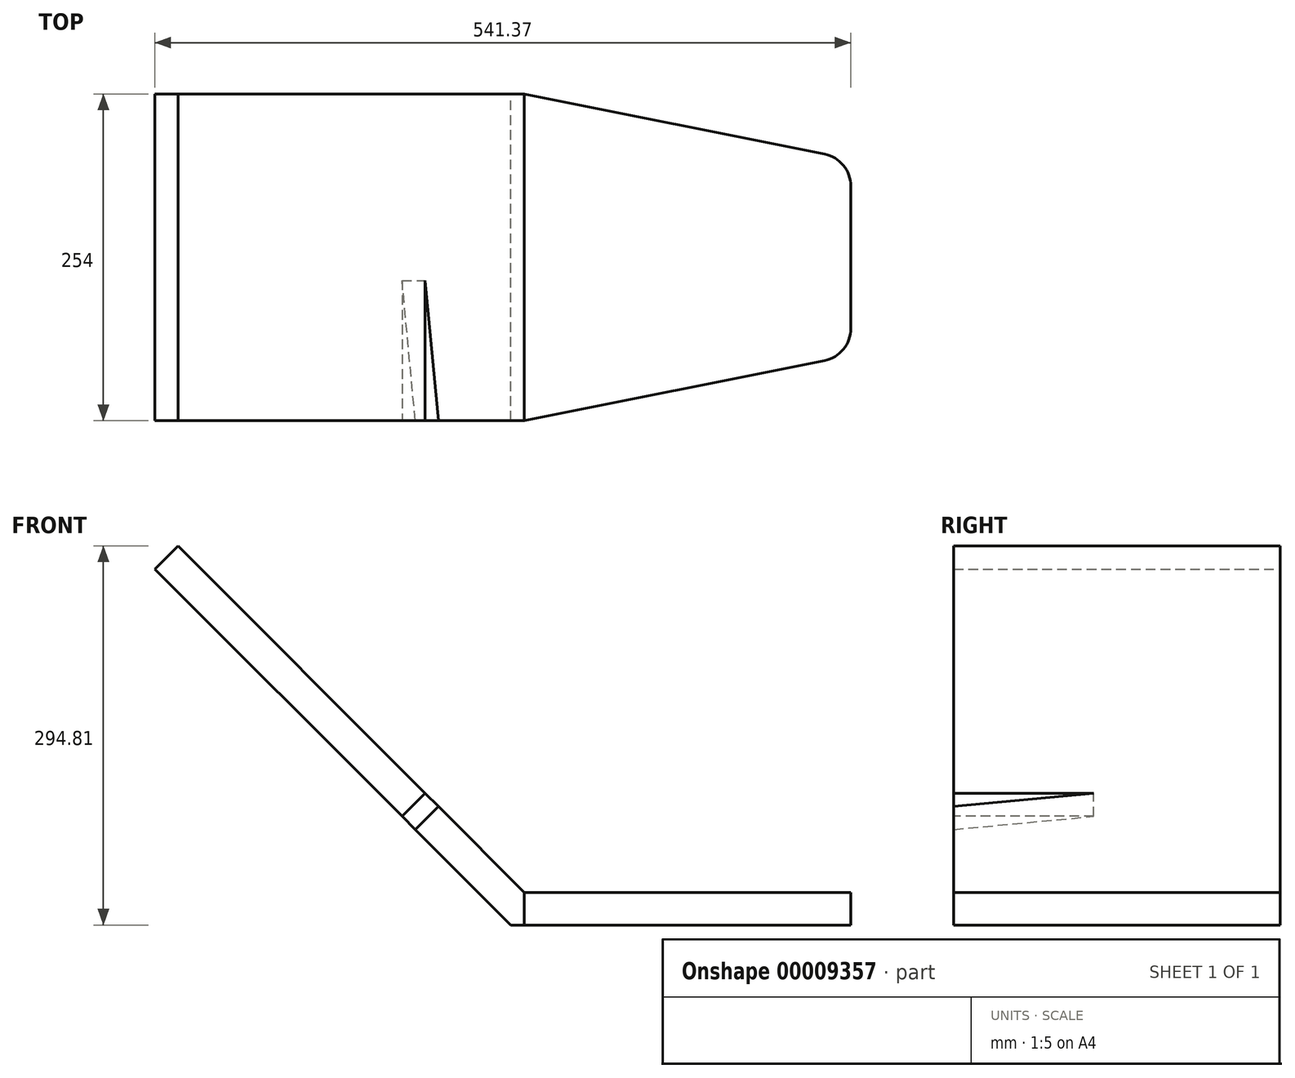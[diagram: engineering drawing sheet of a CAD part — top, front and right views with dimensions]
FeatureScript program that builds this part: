
annotation { "Feature Type Name" : "Feature", "Feature Type Description" : "" }
export const myFeature = defineFeature(function(context is Context, id is Id, definition is map)
    precondition{}
    {
        {
            var Q0;
            Q0=qCreatedBy(makeId("Top.planeOp"),FACE);
            var sketch = newSketch(context, id + "F0", { "sketchPlane" : qUnion([Q0])});
            skLineSegment(sketch, "E0", {"start": v(0, 127) * mm, "end": v(0, -127) * mm});
            skLineSegment(sketch, "E1", {"start": v(0, -127) * mm, "end": v(254, -76.2) * mm});
            skLineSegment(sketch, "E2", {"start": v(254, -76.2) * mm, "end": v(254, 76.2) * mm});
            skLineSegment(sketch, "E3", {"start": v(254, 76.2) * mm, "end": v(0, 127) * mm});
            skSolve(sketch);
        }
        {
            var Q0;
            Q0 = qSketchRegion(id + "F0", true);
            extrude(context, id + "F1", {"entities" : qUnion([Q0]), "depth" : 25.4 * mm});
        }
        {
            var Q0;
            Q0=qCreatedBy(makeId("Front.planeOp"),FACE);
            var sketch = newSketch(context, id + "F2", { "sketchPlane" : qUnion([Q0])});
            skLineSegment(sketch, "E4", {"start": v(0, 25.4) * mm, "end": v(-269.4, 294.8) * mm});
            skLineSegment(sketch, "E5", {"start": v(-269.4, 294.8) * mm, "end": v(-287.37, 276.85) * mm});
            skLineSegment(sketch, "E6", {"start": v(-287.37, 276.85) * mm, "end": v(-10.52, 0) * mm});
            skLineSegment(sketch, "E7", {"start": v(-10.52, 0) * mm, "end": v(0, 0) * mm});
            skLineSegment(sketch, "E8", {"start": v(0, 0) * mm, "end": v(0, 25.4) * mm});
            skSolve(sketch);
        }
        {
            var Q0;
            Q0=makeQuery(id+"F2.imprint","IMPRINT",FACE,{"disambiguationData":[TD([[makeQuery(id+"F2.imprint","IMPRINT",EDGE,{"derivedFrom":sQuery(id+"F2.wireOp",EDGE,"E4")}),1.0]])]});
            var Q1;
            Q1=makeQuery(id+"F1.opExtrude","SWEPT_FACE",FACE,{"disambiguationData":[OSD([sQuery(id+"F0.wireOp",EDGE,"E3")])]});
            extrude(context, id + "F3", {"entities" : qUnion([Q0]), "operationType" : NewBodyOperationType.ADD, "endBound" : BoundingType.SYMMETRIC, "endBoundEntityFace" : qUnion([Q1]), "depth" : 254 * mm});
        }
        {
            var Q0;
            Q0=makeQuery(id+"F3.opExtrude","SWEPT_FACE",FACE,{"disambiguationData":[OSD([sQuery(id+"F2.wireOp",EDGE,"E4")])]});
            var sketch = newSketch(context, id + "F4", { "sketchPlane" : qUnion([Q0])});
            skLineSegment(sketch, "E9", {"start": v(-398.96, 0) * mm, "end": v(-17.96, 0) * mm, "construction": true});
            skLineSegment(sketch, "E10", {"start": v(-398.96, -76.2) * mm, "end": v(-17.96, -127) * mm});
            skLineSegment(sketch, "E11", {"start": v(-17.96, -127) * mm, "end": v(-398.96, -127) * mm});
            skLineSegment(sketch, "E12", {"start": v(-398.96, -127) * mm, "end": v(-398.96, -76.2) * mm});
            skLineSegment(sketch, "E13.MirrorCS", {"start": v(-398.96, 76.2) * mm, "end": v(-17.96, 127) * mm});
            skLineSegment(sketch, "E14.MirrorCS", {"start": v(-398.96, 127) * mm, "end": v(-398.96, 76.2) * mm});
            skLineSegment(sketch, "E15.MirrorCS", {"start": v(-17.96, 127) * mm, "end": v(-398.96, 127) * mm});
            skSolve(sketch);
        }
        {
            var Q0;
            Q0 = qSketchRegion(id + "F4", true);
            extrude(context, id + "F5", {"entities" : qUnion([Q0]), "operationType" : NewBodyOperationType.REMOVE, "endBound" : BoundingType.THROUGH_ALL, "oppositeDirection" : true, "depth" : 25.4 * mm});
        }
        {
            var Q0;
            Q0=makeQuery(id+"F5.boolean.opBoolean","COPY",EDGE,{"derivedFrom":makeQuery(id+"F5.opExtrude","SWEPT_EDGE",EDGE,{"disambiguationData":[OSD([sQuery(id+"F2.wireOp",EDGE,"E4"),sQuery(id+"F2.wireOp",EDGE,"E5"),sQuery(id+"F4.wireOp",EDGE,"E10"),sQuery(id+"F4.wireOp",EDGE,"E12")])]})});
            var Q1;
            Q1=makeQuery(id+"F5.boolean.opBoolean","COPY",EDGE,{"derivedFrom":makeQuery(id+"F5.opExtrude","SWEPT_EDGE",EDGE,{"disambiguationData":[OSD([sQuery(id+"F2.wireOp",EDGE,"E4"),sQuery(id+"F2.wireOp",EDGE,"E5"),sQuery(id+"F4.wireOp",EDGE,"E13.MirrorCS"),sQuery(id+"F4.wireOp",EDGE,"E14.MirrorCS")])]})});
            var Q2;
            Q2=makeQuery(id+"F1.opExtrude","SWEPT_EDGE",EDGE,{"disambiguationData":[OSD([sQuery(id+"F0.wireOp",EDGE,"E1"),sQuery(id+"F0.wireOp",EDGE,"E2")])]});
            var Q3;
            Q3=makeQuery(id+"F1.opExtrude","SWEPT_EDGE",EDGE,{"disambiguationData":[OSD([sQuery(id+"F0.wireOp",EDGE,"E2"),sQuery(id+"F0.wireOp",EDGE,"E3")])]});
            fillet(context, id + "F6", {"entities" : qUnion([Q0, Q1, Q2, Q3]), "radius" : 25.4 * mm, "tangentPropagation" : true, "allowEdgeOverflow" : false});
        }
    });
